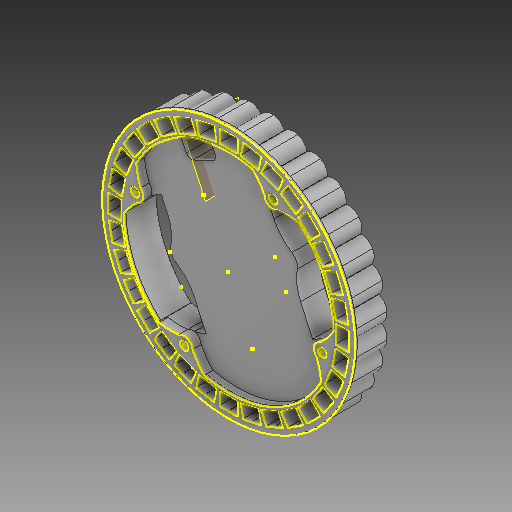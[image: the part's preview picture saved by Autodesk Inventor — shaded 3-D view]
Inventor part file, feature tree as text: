
AUTODESK INVENTOR PART (.ipt)
format: ipt  version: 2020 (Build 240168000, 168)  size: 1,118,208 bytes
history: native  units: mm
features: sketch x10, extrude x7, projected_geometry x3, other x2, hole x2, mirror x1, fillet x1, imported_body x1
ambient origin geometry x8: Origin, YZ Plane, XZ Plane, XY Plane, X Axis, Y Axis, Z Axis, Center Point
bodies: Body1 (feature_tree)
feature tree (27):
  other  "Твердое тело1"
  extrude  "Выдавливание1"  TaperAngle=0.0deg  [1 undecoded]
  sketch  "Эскиз2"
  extrude  "Выдавливание3"  Depth=40.0mm TaperAngle=360.0deg
  sketch  "Эскиз4"
  extrude  "Выдавливание4"  Depth=53.0mm
  extrude  "Выдавливание5"  Depth=82.0mm
  sketch  "Эскиз5"
  hole  "Отверстие1"  [1 undecoded]
  hole  "Отверстие2"  [1 undecoded]
  extrude  "Выдавливание6"  Depth=6.7mm
  other  "РабПлоскость1"
  mirror  "Зеркальное отражение1"
  extrude  "Выдавливание7"  TaperAngle=0.0deg  [1 undecoded]
  fillet  "Сопряжение1"  Radius=20.0mm
  extrude  "Выдавливание8"  Depth=11.0mm TaperAngle=0.0deg
  sketch  "Эскиз10"
  sketch  "Эскиз11"
  sketch  "Эскиз1"
  sketch  "Эскиз3"
  sketch  "Эскиз6"
  sketch  "Эскиз7"
  sketch  "Эскиз8"
  projected_geometry  "Спроецированная петля1"
  projected_geometry  "Спроецированная петля2"
  projected_geometry  "Спроецированная петля3"
  imported_body  "БазТело1"
note: 4 required parameter values undecoded (feature->parameter linkage not recoverable at this tier; creation-order binding heuristic only, values carry confidence <= 0.55)
